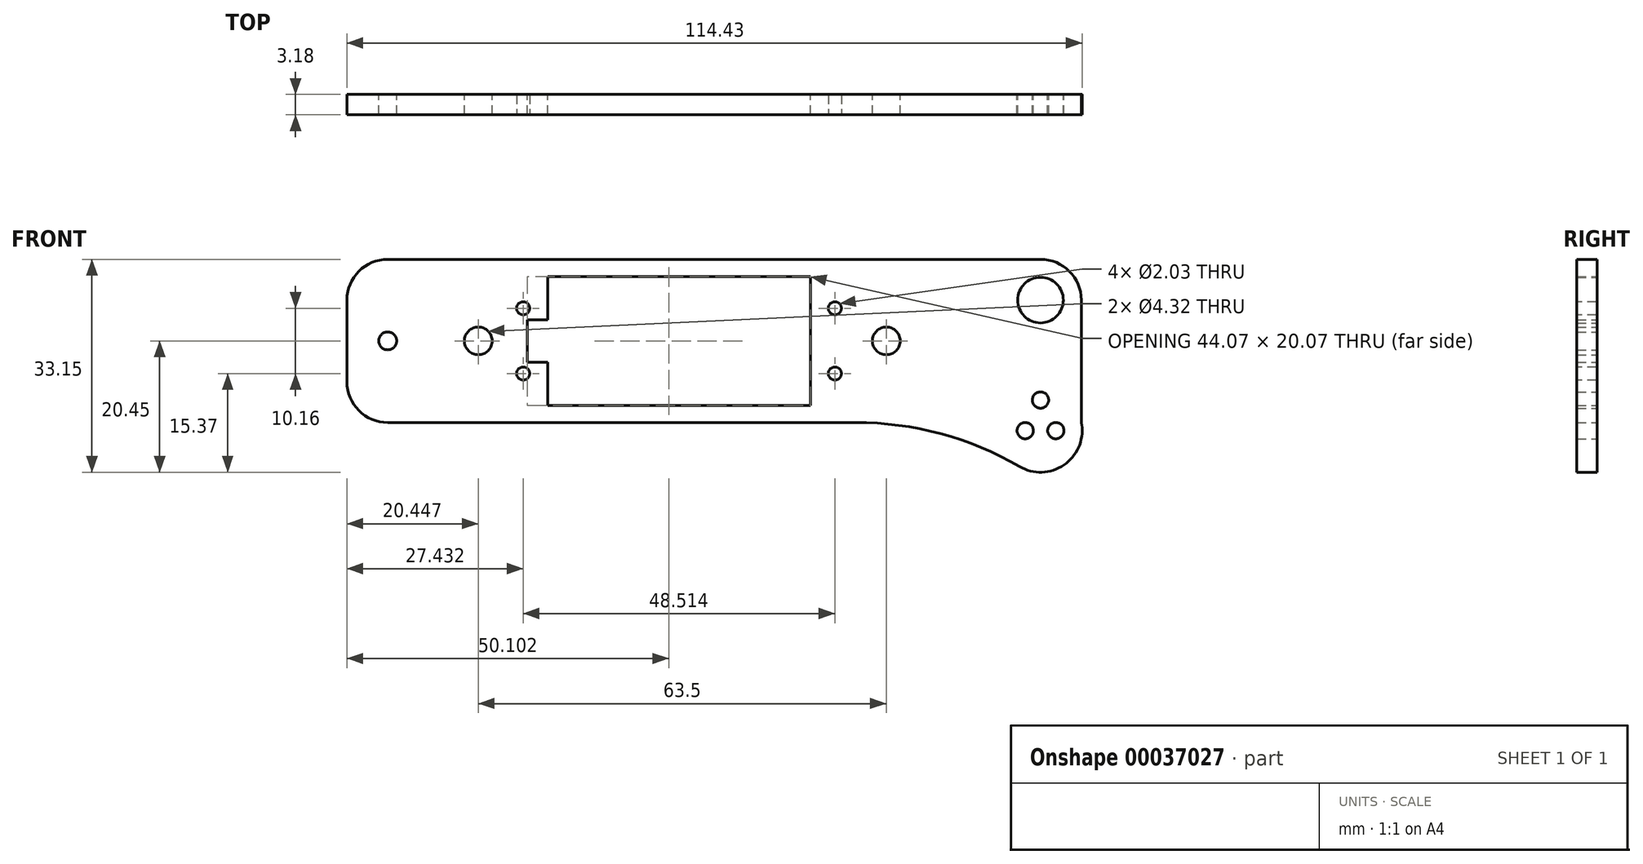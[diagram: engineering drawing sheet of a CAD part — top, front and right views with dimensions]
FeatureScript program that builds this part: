
annotation { "Feature Type Name" : "Feature", "Feature Type Description" : "" }
export const myFeature = defineFeature(function(context is Context, id is Id, definition is map)
    precondition{}
    {
        {
            var Q0;
            Q0=qCreatedBy(makeId("Front.planeOp"),FACE);
            var sketch = newSketch(context, id + "F0", { "sketchPlane" : qUnion([Q0])});
            skLineSegment(sketch, "E0.rect.bottom", {"start": v(57.15, 12.7) * mm, "end": v(-57.15, 12.7) * mm});
            skLineSegment(sketch, "E0.rect.top", {"start": v(57.15, -12.7) * mm, "end": v(-57.15, -12.7) * mm, "construction": true});
            skLineSegment(sketch, "E0.rect.left", {"start": v(57.15, 12.7) * mm, "end": v(57.15, -12.7) * mm});
            skLineSegment(sketch, "E0.rect.right", {"start": v(-57.15, 12.7) * mm, "end": v(-57.15, -12.7) * mm});
            skPoint(sketch, "E0.rect.middle", {"position": v(0, 0) * mm});
            skCircle(sketch, "E1", {"center": v(-50.8, 0) * mm, "radius": 1.4 * mm});
            skCircle(sketch, "E2", {"center": v(50.8, 6.35) * mm, "radius": 3.56 * mm});
            skLineSegment(sketch, "E3", {"start": v(50.8, 6.35) * mm, "end": v(50.8, -13.97) * mm, "construction": true});
            skLineSegment(sketch, "E4", {"start": v(50.8, 0) * mm, "end": v(0, 0) * mm, "construction": true});
            skLineSegment(sketch, "E5.rect.bottom", {"start": v(14.99, 10.03) * mm, "end": v(-25.9, 10.03) * mm});
            skLineSegment(sketch, "E5.rect.top", {"start": v(14.99, -10.03) * mm, "end": v(-25.9, -10.03) * mm});
            skLineSegment(sketch, "E5.rect.left", {"start": v(14.99, 10.03) * mm, "end": v(14.99, -10.03) * mm});
            skLineSegment(sketch, "E5.rect.right", {"start": v(-25.9, 10.03) * mm, "end": v(-25.9, -10.03) * mm, "construction": true});
            skPoint(sketch, "E5.rect.middle", {"position": v(-5.46, 0) * mm});
            skLineSegment(sketch, "E6", {"start": v(-25.9, 10.03) * mm, "end": v(-25.9, 3.3) * mm});
            skLineSegment(sketch, "E7", {"start": v(-25.9, 3.3) * mm, "end": v(-29.08, 3.3) * mm});
            skLineSegment(sketch, "E8", {"start": v(-29.08, 3.3) * mm, "end": v(-29.08, -3.3) * mm});
            skLineSegment(sketch, "E9", {"start": v(-29.08, -3.3) * mm, "end": v(-25.9, -3.3) * mm});
            skLineSegment(sketch, "E10", {"start": v(-25.9, -3.3) * mm, "end": v(-25.9, -10.03) * mm});
            skLineSegment(sketch, "E11", {"start": v(-15.24, 10.03) * mm, "end": v(-15.24, -10.03) * mm, "construction": true});
            skArc(sketch, "E12", {"start": v(57.15, -12.7) * mm, "mid": v(54.57, -19.24) * mm, "end": v(47.55, -19.57) * mm});
            skLineSegment(sketch, "E13", {"start": v(-57.15, -12.7) * mm, "end": v(22.04, -12.7) * mm});
            skPoint(sketch, "E14.visualSharp", {"position": v(44.45, -12.7) * mm});
            skArc(sketch, "E14.filletArc", {"start": v(47.55, -19.57) * mm, "mid": v(35.25, -14.45) * mm, "end": v(22.04, -12.7) * mm});
            skLineSegment(sketch, "E15", {"start": v(48.42, -13.97) * mm, "end": v(53.18, -13.97) * mm, "construction": true});
            skCircle(sketch, "E16", {"center": v(53.18, -13.97) * mm, "radius": 1.27 * mm});
            skCircle(sketch, "E17", {"center": v(48.42, -13.97) * mm, "radius": 1.27 * mm});
            skCircle(sketch, "E18", {"center": v(50.8, -9.2) * mm, "radius": 1.27 * mm});
            skSolve(sketch);
        }
        {
            var Q0;
            Q0 = qSketchRegion(id + "F0", true);
            extrude(context, id + "F1", {"entities" : qUnion([Q0]), "depth" : 3.17 * mm});
        }
        {
            var Q0;
            Q0=makeQuery(id+"F1.opExtrude","CAP_FACE",FACE,{"disambiguationData":[OSD([sQuery(id+"F0.wireOp",EDGE,"E0.rect.bottom"),sQuery(id+"F0.wireOp",EDGE,"E0.rect.top"),sQuery(id+"F0.wireOp",EDGE,"E0.rect.left"),sQuery(id+"F0.wireOp",EDGE,"E0.rect.right"),sQuery(id+"F0.wireOp",EDGE,"E1"),sQuery(id+"F0.wireOp",EDGE,"E2"),sQuery(id+"F0.wireOp",EDGE,"4973b752-d98b-4436-bbf1-77c486dad64a"),sQuery(id+"F0.wireOp",EDGE,"E5.rect.bottom"),sQuery(id+"F0.wireOp",EDGE,"E5.rect.top"),sQuery(id+"F0.wireOp",EDGE,"E5.rect.left"),sQuery(id+"F0.wireOp",EDGE,"E6"),sQuery(id+"F0.wireOp",EDGE,"E7"),sQuery(id+"F0.wireOp",EDGE,"E8"),sQuery(id+"F0.wireOp",EDGE,"E9"),sQuery(id+"F0.wireOp",EDGE,"E10")])],"isStart":false});
            var sketch = newSketch(context, id + "F2", { "sketchPlane" : qUnion([Q0])});
            skLineSegment(sketch, "E19.rect.bottom", {"start": v(18.8, 5.08) * mm, "end": v(-29.72, 5.08) * mm, "construction": true});
            skLineSegment(sketch, "E19.rect.top", {"start": v(18.8, -5.08) * mm, "end": v(-29.72, -5.08) * mm, "construction": true});
            skLineSegment(sketch, "E19.rect.left", {"start": v(18.8, 5.08) * mm, "end": v(18.8, -5.08) * mm, "construction": true});
            skLineSegment(sketch, "E19.rect.right", {"start": v(-29.72, 5.08) * mm, "end": v(-29.72, -5.08) * mm, "construction": true});
            skPoint(sketch, "E19.rect.middle", {"position": v(-5.46, 0) * mm});
            skSolve(sketch);
        }
        {
            var Q0;
            Q0=sQuery(id+"F2.wireOp",VERTEX,"E19.rect.right.start");
            var Q1;
            Q1=sQuery(id+"F2.wireOp",VERTEX,"E19.rect.left.start");
            var Q2;
            Q2=sQuery(id+"F2.wireOp",VERTEX,"E19.rect.left.end");
            var Q3;
            Q3=sQuery(id+"F2.wireOp",VERTEX,"E19.rect.top.end");
            var Q4;
            Q4=makeQuery(id+"F1.opExtrude","SWEPT_BODY",BODY,{"disambiguationData":[OSD([sQuery(id+"F0.wireOp",EDGE,"E0.rect.bottom"),sQuery(id+"F0.wireOp",EDGE,"E0.rect.top"),sQuery(id+"F0.wireOp",EDGE,"E0.rect.left"),sQuery(id+"F0.wireOp",EDGE,"E0.rect.right"),sQuery(id+"F0.wireOp",EDGE,"E1"),sQuery(id+"F0.wireOp",EDGE,"E2"),sQuery(id+"F0.wireOp",EDGE,"4973b752-d98b-4436-bbf1-77c486dad64a"),sQuery(id+"F0.wireOp",EDGE,"E5.rect.bottom"),sQuery(id+"F0.wireOp",EDGE,"E5.rect.top"),sQuery(id+"F0.wireOp",EDGE,"E5.rect.left"),sQuery(id+"F0.wireOp",EDGE,"E6"),sQuery(id+"F0.wireOp",EDGE,"E7"),sQuery(id+"F0.wireOp",EDGE,"E8"),sQuery(id+"F0.wireOp",EDGE,"E9"),sQuery(id+"F0.wireOp",EDGE,"E10")])]});
            hole(context, id + "F3", {"style" : HoleStyle.SIMPLE, "holeDiameter" : 2.03 * mm, "endStyle" : HoleEndStyle.THROUGH, "locations" : qUnion([Q0, Q1, Q2, Q3]), "scope" : qUnion([Q4])});
        }
        {
            var Q0;
            Q0=qCreatedBy(makeId("Front.planeOp"),FACE);
            var sketch = newSketch(context, id + "F4", { "sketchPlane" : qUnion([Q0])});
            skLineSegment(sketch, "E20", {"start": v(-36.7, 0) * mm, "end": v(26.8, 0) * mm, "construction": true});
            skSolve(sketch);
        }
        {
            var Q0;
            Q0=sQuery(id+"F4.wireOp",VERTEX,"E20.start");
            var Q1;
            Q1=sQuery(id+"F4.wireOp",VERTEX,"E20.end");
            var Q2;
            Q2=makeQuery(id+"F1.opExtrude","SWEPT_BODY",BODY,{"disambiguationData":[OSD([sQuery(id+"F0.wireOp",EDGE,"E0.rect.bottom"),sQuery(id+"F0.wireOp",EDGE,"E0.rect.top"),sQuery(id+"F0.wireOp",EDGE,"E0.rect.left"),sQuery(id+"F0.wireOp",EDGE,"E0.rect.right"),sQuery(id+"F0.wireOp",EDGE,"E1"),sQuery(id+"F0.wireOp",EDGE,"E2"),sQuery(id+"F0.wireOp",EDGE,"4973b752-d98b-4436-bbf1-77c486dad64a"),sQuery(id+"F0.wireOp",EDGE,"E5.rect.bottom"),sQuery(id+"F0.wireOp",EDGE,"E5.rect.top"),sQuery(id+"F0.wireOp",EDGE,"E5.rect.left"),sQuery(id+"F0.wireOp",EDGE,"E6"),sQuery(id+"F0.wireOp",EDGE,"E7"),sQuery(id+"F0.wireOp",EDGE,"E8"),sQuery(id+"F0.wireOp",EDGE,"E9"),sQuery(id+"F0.wireOp",EDGE,"E10")])]});
            hole(context, id + "F5", {"style" : HoleStyle.SIMPLE, "holeDiameter" : 4.32 * mm, "endStyle" : HoleEndStyle.THROUGH, "oppositeDirection" : true, "locations" : qUnion([Q0, Q1]), "scope" : qUnion([Q2])});
        }
        {
            var Q0;
            Q0=makeQuery(id+"F1.opExtrude","SWEPT_EDGE",EDGE,{"disambiguationData":[OSD([sQuery(id+"F0.wireOp",EDGE,"E0.rect.bottom"),sQuery(id+"F0.wireOp",EDGE,"E0.rect.right")])]});
            var Q1;
            Q1=makeQuery(id+"F1.opExtrude","SWEPT_EDGE",EDGE,{"disambiguationData":[OSD([sQuery(id+"F0.wireOp",EDGE,"E0.rect.top"),sQuery(id+"F0.wireOp",EDGE,"E0.rect.right")])]});
            var Q2;
            Q2=makeQuery(id+"F1.opExtrude","SWEPT_EDGE",EDGE,{"disambiguationData":[OSD([sQuery(id+"F0.wireOp",EDGE,"E0.rect.bottom"),sQuery(id+"F0.wireOp",EDGE,"E0.rect.left")])]});
            var Q3;
            Q3=makeQuery(id+"F1.opExtrude","SWEPT_EDGE",EDGE,{"disambiguationData":[OSD([sQuery(id+"F0.wireOp",EDGE,"E0.rect.top"),sQuery(id+"F0.wireOp",EDGE,"E0.rect.left")])]});
            fillet(context, id + "F6", {"entities" : qUnion([Q0, Q1, Q2, Q3]), "radius" : 6.35 * mm, "tangentPropagation" : true, "allowEdgeOverflow" : false});
        }
    });
